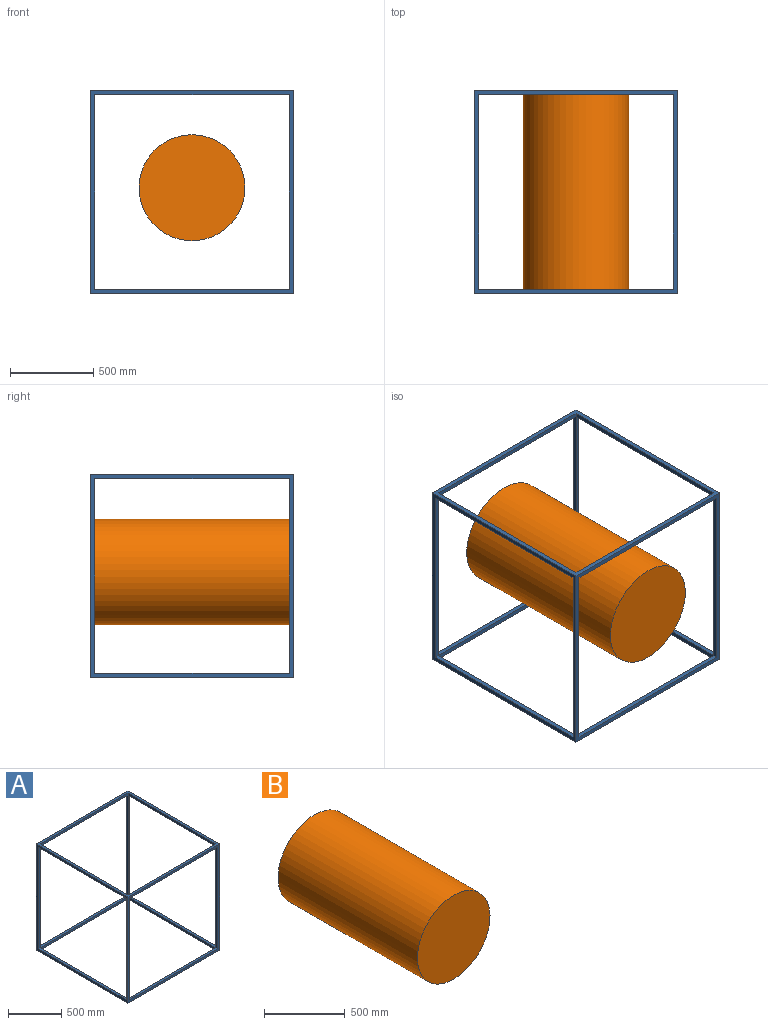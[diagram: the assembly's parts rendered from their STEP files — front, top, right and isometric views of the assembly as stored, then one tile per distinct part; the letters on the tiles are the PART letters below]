
ASSEMBLY  parts=2 mates=2
PART A: 30 faces, bbox 1219.2x1219.2x1219.2 mm
  f0: plane 1168.4x25.4mm, normal (1,0,0), area 29677.4mm2, adj f7,f18,f19,f26
  f1: plane 1168.4x25.4mm, normal (1,0,0), area 29677.4mm2, adj f11,f15,f17,f28
  f2: plane 1168.4x25.4mm, normal (1,0,0), area 29677.4mm2, adj f6,f20,f21,f29
  f3: plane 1168.4x25.4mm, normal (-1,0,0), area 29677.4mm2, adj f7,f18,f19,f25
  f4: plane 1168.4x25.4mm, normal (-1,0,0), area 29677.4mm2, adj f11,f15,f17,f23
  f5: plane 1168.4x25.4mm, normal (-1,0,0), area 29677.4mm2, adj f6,f20,f21,f22
  f6: plane 1219.2x1219.2mm, normal (0,1,0), area 121290.1mm2, adj f2,f5,f10,f11,f12,f13,f20,f21
  f7: plane 1219.2x1219.2mm, normal (0,-1,0), area 121290.1mm2, adj f0,f3,f10,f11,f12,f13,f18,f19
  f8: plane 1168.4x25.4mm, normal (0,-1,0), area 29677.4mm2, adj f10,f14,f16,f20
  f9: plane 1168.4x25.4mm, normal (0,1,0), area 29677.4mm2, adj f10,f14,f16,f19
  f10: plane 1219.2x1219.2mm, normal (0,0,1), area 121290.1mm2, adj f6,f7,f8,f9,f12,f13,f14,f16
  f11: plane 1219.2x1219.2mm, normal (0,0,-1), area 121290.1mm2, adj f1,f4,f6,f7,f12,f13,f15,f17
  f12: plane 1219.2x1219.2mm, normal (-1,0,0), area 121290.1mm2, adj f6,f7,f10,f11,f26,f27,f28,f29
  f13: plane 1219.2x1219.2mm, normal (1,0,0), area 121290.1mm2, adj f6,f7,f10,f11,f22,f23,f24,f25
  f14: plane 1168.4x25.4mm, normal (1,0,0), area 29677.4mm2, adj f8,f9,f10,f27
  f15: plane 1168.4x25.4mm, normal (0,-1,0), area 29677.4mm2, adj f1,f4,f11,f21
  f16: plane 1168.4x25.4mm, normal (-1,0,0), area 29677.4mm2, adj f8,f9,f10,f24
  f17: plane 1168.4x25.4mm, normal (0,1,0), area 29677.4mm2, adj f1,f4,f11,f18
  f18: plane 1168.4x25.4mm, normal (0,0,1), area 29677.4mm2, adj f0,f3,f7,f17
  f19: plane 1168.4x25.4mm, normal (0,0,-1), area 29677.4mm2, adj f0,f3,f7,f9
  f20: plane 1168.4x25.4mm, normal (0,0,-1), area 29677.4mm2, adj f2,f5,f6,f8
  f21: plane 1168.4x25.4mm, normal (0,0,1), area 29677.4mm2, adj f2,f5,f6,f15
  f22: plane 1168.4x25.4mm, normal (0,-1,0), area 29677.4mm2, adj f5,f13,f23,f24
  f23: plane 1168.4x25.4mm, normal (0,0,1), area 29677.4mm2, adj f4,f13,f22,f25
  f24: plane 1168.4x25.4mm, normal (0,0,-1), area 29677.4mm2, adj f13,f16,f22,f25
  f25: plane 1168.4x25.4mm, normal (0,1,0), area 29677.4mm2, adj f3,f13,f23,f24
  f26: plane 1168.4x25.4mm, normal (0,1,0), area 29677.4mm2, adj f0,f12,f27,f28
  f27: plane 1168.4x25.4mm, normal (0,0,-1), area 29677.4mm2, adj f12,f14,f26,f29
  f28: plane 1168.4x25.4mm, normal (0,0,1), area 29677.4mm2, adj f1,f12,f26,f29
  f29: plane 1168.4x25.4mm, normal (0,-1,0), area 29677.4mm2, adj f2,f12,f27,f28
PART B: 3 faces, bbox 635x1219.2x635 mm
  f0: cylinder r=317.5mm len=1219.2mm, axis (0,1,0), area 2432195.9mm2, adj f1,f2
  f1: plane 635x635mm, normal (0,-1,0), area 316692.2mm2, adj f0
  f2: plane 635x635mm, normal (0,1,0), area 316692.2mm2, adj f0
PLACE A t=(-93.62,-63.76,50.89)mm
PLACE B t=(434.36,1119.27,685.89)mm
MATE fastened B.f0 <-> A.f7  axis (0,-1,0) through (434.36,-99.93,685.89)mm
MATE planar B.f0 <-> A.f7  axis (0,-1,0) through (434.36,-99.93,685.89)mm
